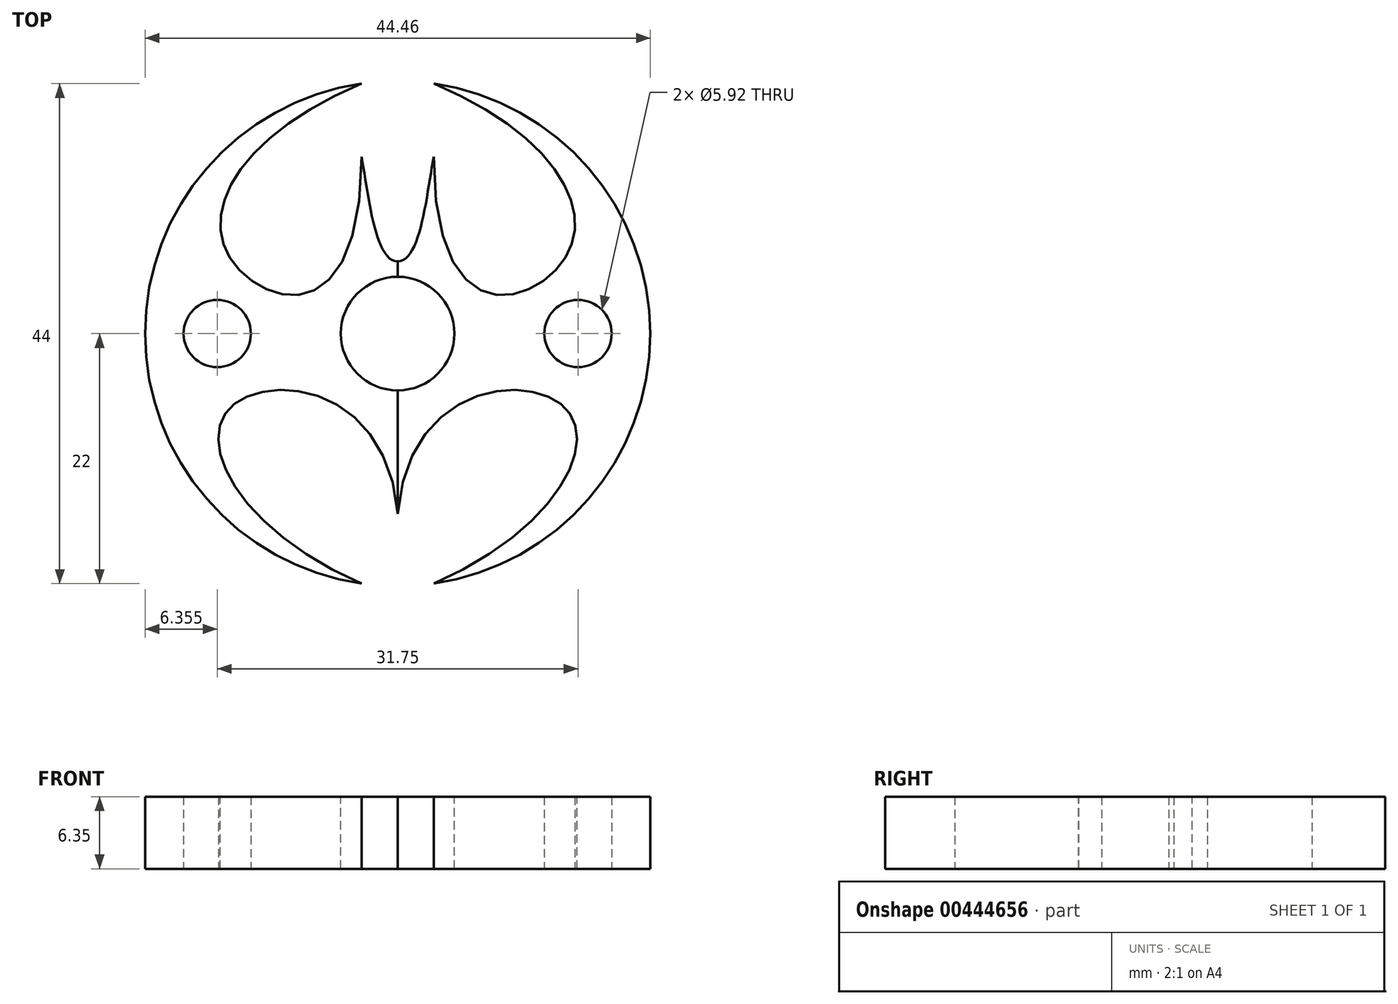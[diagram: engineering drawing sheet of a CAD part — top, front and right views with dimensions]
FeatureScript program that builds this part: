
annotation { "Feature Type Name" : "Feature", "Feature Type Description" : "" }
export const myFeature = defineFeature(function(context is Context, id is Id, definition is map)
    precondition{}
    {
        {
            var Q0;
            Q0=qCreatedBy(makeId("Top.planeOp"),FACE);
            var sketch = newSketch(context, id + "F0", { "sketchPlane" : qUnion([Q0])});
            skLineSegment(sketch, "E0", {"start": v(0, 47.4) * mm, "end": v(0, -68.44) * mm, "construction": true});
            skCircle(sketch, "E1", {"center": v(0, 0) * mm, "radius": 22.23 * mm, "construction": true});
            skCircle(sketch, "E2", {"center": v(0, 0) * mm, "radius": 9.53 * mm, "construction": true});
            skLineSegment(sketch, "E3", {"start": v(-24.41, 9.53) * mm, "end": v(28.44, 9.53) * mm, "construction": true});
            skLineSegment(sketch, "E4", {"start": v(-24.41, -9.53) * mm, "end": v(28.44, -9.53) * mm, "construction": true});
            skCircle(sketch, "E5", {"center": v(0, 0) * mm, "radius": 15.88 * mm, "construction": true});
            skLineSegment(sketch, "E6", {"start": v(-24.41, 6.35) * mm, "end": v(28.84, 6.35) * mm, "construction": true});
            skLineSegment(sketch, "E7", {"start": v(-24.41, -6.35) * mm, "end": v(28.84, -6.35) * mm, "construction": true});
            skLineSegment(sketch, "E8", {"start": v(-3.17, 24) * mm, "end": v(-3.17, -23.12) * mm, "construction": true});
            skArc(sketch, "E9", {"start": v(-3.18, 22) * mm, "mid": v(-22.22, 0) * mm, "end": v(-3.17, -22) * mm});
            skLineSegment(sketch, "E10", {"start": v(-31.03, 0) * mm, "end": v(33.17, 0) * mm, "construction": true});
            skFitSpline(sketch, "E11", {"points": [v(-3.17, 22) * mm, v(-14.55, 6.35) * mm, v(-3.17, 15.55) * mm], "startDerivative": vector(-57.75, -24.23) * mm, "endDerivative": vector(0, 100.32) * mm});
            skFitSpline(sketch, "E12", {"points": [v(-3.17, -22) * mm, v(-14.55, -6.35) * mm, v(0, -15.88) * mm], "startDerivative": vector(-62.67, 27.2) * mm, "endDerivative": vector(5.38, -69.47) * mm});
            skFitSpline(sketch, "E13", {"points": [v(-3.17, 15.55) * mm, v(0, 6.35) * mm], "startDerivative": vector(1.99, -10.67) * mm, "endDerivative": vector(6.02, 0) * mm});
            skLineSegment(sketch, "E14", {"start": v(0, 6.35) * mm, "end": v(0, -15.88) * mm});
            skCircle(sketch, "E15", {"center": v(-15.88, 0) * mm, "radius": 2.96 * mm});
            skSolve(sketch);
        }
        {
            var Q0;
            Q0 = qSketchRegion(id + "F0", true);
            extrude(context, id + "F1", {"entities" : qUnion([Q0]), "depth" : 6.35 * mm});
        }
        {
            var Q0;
            Q0=makeQuery(id+"F1.opExtrude","SWEPT_BODY",BODY,{"disambiguationData":[OSD([sQuery(id+"F0.wireOp",EDGE,"E9"),sQuery(id+"F0.wireOp",EDGE,"E11"),sQuery(id+"F0.wireOp",EDGE,"E12"),sQuery(id+"F0.wireOp",EDGE,"E13"),sQuery(id+"F0.wireOp",EDGE,"E14")])]});
            var Q1;
            Q1=makeQuery(id+"F1.opExtrude","SWEPT_FACE",FACE,{"disambiguationData":[OSD([sQuery(id+"F0.wireOp",EDGE,"E14")])]});
            mirror(context, id + "F2", {"entities" : qUnion([Q0]), "mirrorPlane" : qUnion([Q1])});
        }
        {
            var Q0;
            Q0=makeQuery(id+"F1.opExtrude","CAP_FACE",FACE,{"disambiguationData":[OSD([sQuery(id+"F0.wireOp",EDGE,"E9"),sQuery(id+"F0.wireOp",EDGE,"E11"),sQuery(id+"F0.wireOp",EDGE,"E12"),sQuery(id+"F0.wireOp",EDGE,"E13"),sQuery(id+"F0.wireOp",EDGE,"E14")])],"isStart":false});
            var sketch = newSketch(context, id + "F3", { "sketchPlane" : qUnion([Q0])});
            skCircle(sketch, "E16", {"center": v(0, 0) * mm, "radius": 4.6 * mm});
            skLineSegment(sketch, "E17", {"start": v(-29.74, 0) * mm, "end": v(37.43, 0) * mm, "construction": true});
            skCircle(sketch, "E18", {"center": v(-16.85, 0) * mm, "radius": 3 * mm, "construction": true});
            skSolve(sketch);
        }
        {
            var Q0;
            Q0=sQuery(id+"F3.wireOp",VERTEX,"E16.center");
            var Q1;
            Q1=makeQuery(id+"F1.opExtrude","SWEPT_BODY",BODY,{"disambiguationData":[OSD([sQuery(id+"F0.wireOp",EDGE,"E9"),sQuery(id+"F0.wireOp",EDGE,"E11"),sQuery(id+"F0.wireOp",EDGE,"E12"),sQuery(id+"F0.wireOp",EDGE,"E13"),sQuery(id+"F0.wireOp",EDGE,"E14")])]});
            var Q2;
            Q2=makeQuery(id+"F2.opPattern","COPY",BODY,{"derivedFrom":makeQuery(id+"F1.opExtrude","SWEPT_BODY",BODY,{"disambiguationData":[OSD([sQuery(id+"F0.wireOp",EDGE,"E9"),sQuery(id+"F0.wireOp",EDGE,"E11"),sQuery(id+"F0.wireOp",EDGE,"E12"),sQuery(id+"F0.wireOp",EDGE,"E13"),sQuery(id+"F0.wireOp",EDGE,"E14")])]}),"instanceName":"1"});
            hole(context, id + "F4", {"style" : HoleStyle.SIMPLE, "endStyle" : HoleEndStyle.THROUGH, "holeDiameter" : 10 * mm, "isTappedThrough" : true, "tappedDepth" : 12.7 * mm, "tapClearance" : 3, "startFromSketch" : true, "locations" : qUnion([Q0]), "scope" : qUnion([Q1, Q2])});
        }
    });
